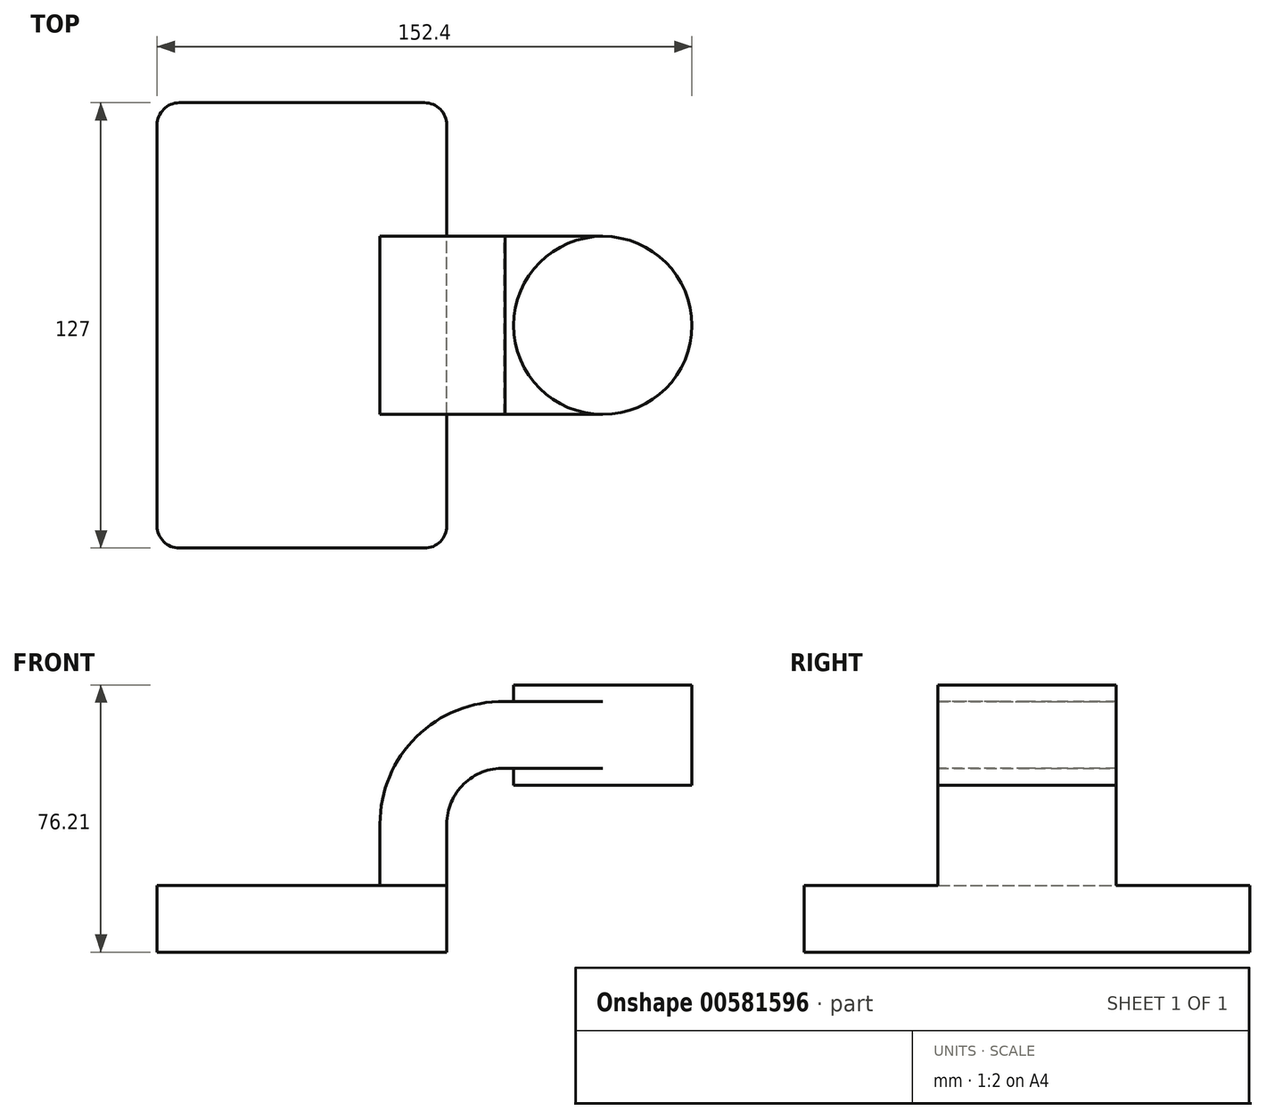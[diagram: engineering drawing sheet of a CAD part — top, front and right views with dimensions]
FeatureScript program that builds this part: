
annotation { "Feature Type Name" : "Feature", "Feature Type Description" : "" }
export const myFeature = defineFeature(function(context is Context, id is Id, definition is map)
    precondition{}
    {
        {
            var Q0;
            Q0=qCreatedBy(makeId("Front.planeOp"),FACE);
            var sketch = newSketch(context, id + "F0", { "sketchPlane" : qUnion([Q0])});
            skLineSegment(sketch, "E0.bottom", {"start": v(41.28, -9.52) * mm, "end": v(-41.27, -9.52) * mm});
            skLineSegment(sketch, "E0.top", {"start": v(41.27, 9.53) * mm, "end": v(-41.28, 9.53) * mm});
            skLineSegment(sketch, "E0.left", {"start": v(41.28, -9.52) * mm, "end": v(41.28, 9.53) * mm});
            skLineSegment(sketch, "E0.right", {"start": v(-41.27, -9.52) * mm, "end": v(-41.28, 9.53) * mm});
            skPoint(sketch, "E0.middle", {"position": v(0, 0) * mm});
            skLineSegment(sketch, "E1.bottom", {"start": v(111.13, 66.68) * mm, "end": v(60.33, 66.68) * mm});
            skLineSegment(sketch, "E1.top", {"start": v(111.13, 38.1) * mm, "end": v(60.33, 38.1) * mm});
            skLineSegment(sketch, "E1.left", {"start": v(111.13, 66.68) * mm, "end": v(111.13, 38.1) * mm});
            skLineSegment(sketch, "E1.right", {"start": v(60.33, 66.68) * mm, "end": v(60.33, 38.1) * mm});
            skPoint(sketch, "E1.middle", {"position": v(85.73, 52.39) * mm});
            skLineSegment(sketch, "E2", {"start": v(41.27, 9.53) * mm, "end": v(41.27, 27) * mm});
            skArc(sketch, "E3", {"start": v(41.27, 27) * mm, "mid": v(46.1, 38.4) * mm, "end": v(57.63, 42.88) * mm});
            skLineSegment(sketch, "E4", {"start": v(57.63, 42.88) * mm, "end": v(85.72, 42.88) * mm});
            skLineSegment(sketch, "E5.0", {"start": v(57.86, 61.93) * mm, "end": v(85.73, 61.93) * mm});
            skArc(sketch, "E5.1", {"start": v(22.23, 27) * mm, "mid": v(32.7, 51.95) * mm, "end": v(57.86, 61.93) * mm});
            skLineSegment(sketch, "E5.2", {"start": v(22.22, 9.53) * mm, "end": v(22.22, 27) * mm});
            skPoint(sketch, "E6", {"position": v(85.73, 66.68) * mm});
            skLineSegment(sketch, "E7", {"start": v(85.73, 38.1) * mm, "end": v(85.73, 66.68) * mm});
            skFitSpline(sketch, "E8", {"points": [v(-41.28, 9.52) * mm, v(57.86, 61.93) * mm], "startDerivative": vector(2.35, 103.2) * mm, "endDerivative": vector(155.83, -2.84) * mm});
            skSolve(sketch);
        }
        {
            var Q0;
            Q0=makeQuery(id+"F0.imprint","IMPRINT",FACE,{"disambiguationData":[TD([[makeQuery(id+"F0.imprint","IMPRINT",EDGE,{"derivedFrom":sQuery(id+"F0.wireOp",EDGE,"E0.bottom")}),-1.0]])]});
            extrude(context, id + "F1", {"entities" : qUnion([Q0]), "endBound" : BoundingType.SYMMETRIC, "depth" : 127 * mm, "offsetDistance" : 25.4 * mm});
        }
        {
            var Q0;
            {var subQ0=sQuery(id+"F0.wireOp",EDGE,"E5.0");var subQ1=sQuery(id+"F0.wireOp",EDGE,"E1.right");var subQ2=makeQuery(id+"F0.imprint","INTERSECT",VERTEX,{"derivedFrom":[subQ1,subQ0]});Q0=makeQuery(id+"F0.imprint","IMPRINT",FACE,{"disambiguationData":[TD([[makeQuery(id+"F0.imprint","IMPRINT",EDGE,{"disambiguationData":[TD([[subQ2,-1.0]])],"derivedFrom":subQ1}),1.0]])]});}
            var Q1;
            {var subQ5=sQuery(id+"F0.wireOp",EDGE,"E2");Q1=makeQuery(id+"F0.imprint","IMPRINT",FACE,{"disambiguationData":[TD([[makeQuery(id+"F0.imprint","IMPRINT",EDGE,{"derivedFrom":subQ5}),1.0]])]});}
            extrude(context, id + "F2", {"entities" : qUnion([Q0, Q1]), "operationType" : NewBodyOperationType.ADD, "endBound" : BoundingType.SYMMETRIC, "depth" : 50.8 * mm, "offsetDistance" : 25.4 * mm});
        }
        {
            var Q0;
            {var subQ4=sQuery(id+"F0.wireOp",EDGE,"E5.1");Q0=makeQuery(id+"F0.imprint","IMPRINT",FACE,{"disambiguationData":[TD([[makeQuery(id+"F0.imprint","IMPRINT",EDGE,{"derivedFrom":subQ4}),1.0]])]});}
            extrude(context, id + "F3", {"entities" : qUnion([Q0]), "operationType" : NewBodyOperationType.ADD, "endBound" : BoundingType.SYMMETRIC, "depth" : 15.88 * mm, "offsetDistance" : 25.4 * mm});
        }
        {
            var Q0;
            {var subQ4=sQuery(id+"F0.wireOp",EDGE,"E1.left");Q0=makeQuery(id+"F0.imprint","IMPRINT",FACE,{"disambiguationData":[TD([[makeQuery(id+"F0.imprint","IMPRINT",EDGE,{"derivedFrom":subQ4}),-1.0]])]});}
            var Q1;
            Q1=sQuery(id+"F0.wireOp",EDGE,"E7");
            revolve(context, id + "F4", {"operationType" : NewBodyOperationType.ADD, "entities" : qUnion([Q0]), "axis" : qUnion([Q1]), "revolveType" : RevolveType.FULL});
        }
        {
            var Q0;
            Q0=makeQuery(id+"F1.opExtrude","CAP_EDGE",EDGE,{"disambiguationData":[OSD([sQuery(id+"F0.wireOp",EDGE,"E0.left")])],"isStart":false});
            var Q1;
            Q1=makeQuery(id+"F1.opExtrude","CAP_EDGE",EDGE,{"disambiguationData":[OSD([sQuery(id+"F0.wireOp",EDGE,"E0.right")])],"isStart":false});
            var Q2;
            Q2=makeQuery(id+"F1.opExtrude","CAP_EDGE",EDGE,{"disambiguationData":[OSD([sQuery(id+"F0.wireOp",EDGE,"E0.left")])],"isStart":true});
            var Q3;
            Q3=makeQuery(id+"F1.opExtrude","CAP_EDGE",EDGE,{"disambiguationData":[OSD([sQuery(id+"F0.wireOp",EDGE,"E0.right")])],"isStart":true});
            fillet(context, id + "F5", {"entities" : qUnion([Q0, Q1, Q2, Q3]), "radius" : 6.35 * mm, "tangentPropagation" : true, "allowEdgeOverflow" : false});
        }
    });
